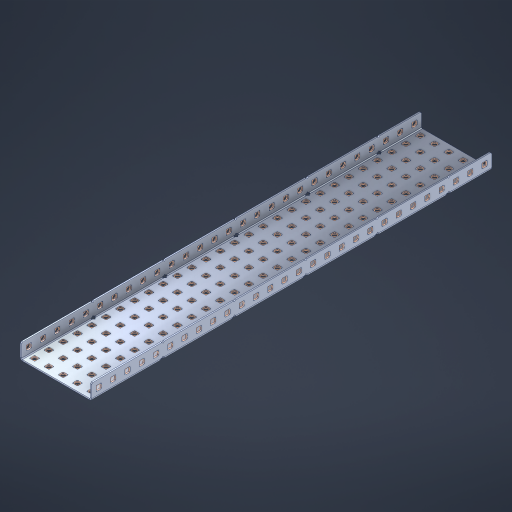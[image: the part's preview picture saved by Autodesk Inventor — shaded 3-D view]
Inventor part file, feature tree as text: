
AUTODESK INVENTOR PART (.ipt)
format: ipt  version: 2023 (Build 270158000, 158)  size: 2,155,008 bytes
history: native  units: in
note: dims shown in document units (in); Inventor stores cm internally (conversion verified against a paired STEP export)
features: other x201, extrude x195, sheet_metal_op x10, sketch x8, mirror x1, pattern_linear x1, chamfer x1
ambient origin geometry x8: Origin, YZ Plane, XZ Plane, XY Plane, X Axis, Y Axis, Z Axis, Center Point
bodies: Solid1 (feature_tree), Body (feature_tree)
feature tree (417):
  other  "Flange Pattern Plane"
  sheet_metal_op  "Flange Pattern"
  sheet_metal_op  "Body Pattern"
  other  "Arc Length"
  mirror  "Notch Mirror"
  pattern_linear  "Notch Pattern"  Spacing1=0.1875in  [1 undecoded]
  chamfer  "End Chamfer"
  extrude  "Half Cut"  Depth=0.0469in
  sketch  "Sketch1"  dims[d0=2.5in]
  other  "Plate1"
  sketch  "Sketch2"  dims[d1=14.0in]
  other  "Plate2"
  sheet_metal_op  "Bend1"
  sheet_metal_op  "Corner1"
  sketch  "Sketch3"  dims[d2=0.0469in]
  other  "Flange Pattern Sketch"
  sketch  "Sketch7"  dims[d3=0.0469in]
  other  "Srf1"
  other  "Srf2"
  sketch  "Sketch8"  dims[d4=0.0234in]
  sketch  "Sketch9"  dims[d5=0.0938in]
  other  "Srf91"
  sheet_metal_op  "Body Pattern Sketch"
  other  "Srf92"
  sketch  "Sketch13"  dims[d6=0.0469in]
  sketch  "Sketch14"  dims[d7=0.5in d8=90.0deg d9=0.0312in d10=0.1875in d11=0.0469in d12=0.0469in d16=0.182in d17=0.02in d18=0.0469in d19=0.0in d20=0.25in d21=0.25in d46=0.172in d47=1.0in d48=0.0in d49=0.182in d50=0.02in d51=0.25in d52=0.25in d53=0.0469in d54=0.0in d55=0.172in d56=1.0in d57=0.0in d60=11.0236in d62=0.5in d63=1.9685in d65=0.5in d85=0.1227in d86=0.1659in d88=0.04in d89=0.0469in d90=0.0in d91=0.04in d92=0.0491in d95=2.5in d96=0.04in d97=0.25in d98=45.0deg d101=0.0in d102=2.497in d131=2.5in d132=11.0236in d134=0.5in d139=0.5in]
  other  "Srf856"
  other  "Srf1310"
  other  "Srf1311"
  other  "Srf1312"
  other  "Srf1376"
  other  "Srf1377"
  other  "Srf1728"
  other  "Srf1755"
  other  "Srf1878"
  other  "Srf1879"
  other  "Srf1880"
  other  "Srf1881"
  other  "Srf1882"
  other  "Srf1883"
  other  "Srf1884"
  other  "Srf1885"
  other  "Srf1886"
  other  "Srf1887"
  other  "Srf1888"
  other  "Srf1889"
  other  "Srf1890"
  other  "Srf1891"
  other  "Srf1892"
  other  "Srf1893"
  other  "Srf1894"
  other  "Srf1895"
  other  "Srf1896"
  other  "Srf1897"
  other  "Srf1898"
  other  "Srf1899"
  other  "Srf1900"
  other  "Srf1901"
  other  "Srf1902"
  other  "Srf1903"
  other  "Srf1904"
  other  "Srf1905"
  other  "Srf1906"
  other  "Srf1942"
  other  "Srf1943"
  other  "Srf1944"
  other  "Srf1945"
  other  "Srf1946"
  other  "Srf1947"
  other  "Srf1948"
  other  "Srf1949"
  other  "Srf1950"
  other  "Srf1951"
  other  "Srf1952"
  other  "Srf1953"
  other  "Srf1954"
  other  "Srf1955"
  other  "Srf1956"
  other  "Srf1957"
  other  "Srf1958"
  other  "Srf1959"
  other  "Srf1960"
  other  "Srf1961"
  other  "Srf1962"
  other  "Srf1963"
  other  "Srf1964"
  other  "Srf1965"
  other  "Srf1966"
  other  "Srf1967"
  other  "Srf1968"
  other  "Srf1969"
  other  "Srf1970"
  other  "Srf2111"
  other  "Srf2112"
  other  "Srf2113"
  other  "Srf2114"
  other  "Srf2115"
  other  "Srf2116"
  other  "Srf2117"
  other  "Srf2118"
  other  "Srf2119"
  other  "Srf2120"
  other  "Srf2121"
  other  "Srf2122"
  other  "Srf2123"
  other  "Srf2124"
  other  "Srf2125"
  other  "Srf2126"
  other  "Srf2127"
  other  "Srf2128"
  other  "Srf2129"
  other  "Srf2130"
  other  "Srf2131"
  other  "Srf2146"
  other  "Srf2147"
  other  "Srf2148"
  other  "Srf2149"
  other  "Srf2150"
  other  "Srf2151"
  other  "Srf2152"
  other  "Srf2153"
  other  "Srf2154"
  other  "Srf2155"
  other  "Srf2156"
  other  "Srf2157"
  other  "Srf2158"
  other  "Srf2159"
  other  "Srf2160"
  other  "Srf2161"
  other  "Srf2162"
  other  "Srf2163"
  other  "Srf2164"
  other  "Srf2165"
  other  "Srf2166"
  other  "Srf2167"
  other  "Srf2168"
  other  "Srf2169"
  other  "Srf2170"
  other  "Srf2171"
  other  "Srf2172"
  other  "Srf2173"
  other  "Srf2174"
  other  "Srf2175"
  other  "Srf2176"
  other  "Srf2177"
  other  "Srf2178"
  other  "Srf2179"
  other  "Srf2180"
  other  "Srf2181"
  other  "Srf2182"
  other  "Srf2183"
  other  "Srf2184"
  other  "Srf2185"
  other  "Srf2186"
  other  "Srf2187"
  other  "Srf2188"
  other  "Srf2189"
  other  "Srf2190"
  other  "Srf2191"
  other  "Srf2192"
  other  "Srf2193"
  other  "Srf2194"
  other  "Srf2195"
  other  "Srf2196"
  other  "Srf2197"
  other  "Srf2198"
  other  "Srf2199"
  other  "Srf2200"
  other  "Srf2201"
  other  "Srf2202"
  other  "Srf2203"
  other  "Srf2204"
  other  "Srf2205"
  other  "Srf2206"
  other  "Srf2207"
  other  "Srf2208"
  other  "Srf2209"
  other  "Srf2210"
  other  "Srf2211"
  other  "Srf2212"
  other  "Srf2213"
  other  "Srf2214"
  other  "Srf2215"
  other  "Srf2216"
  other  "Srf2217"
  other  "Srf2218"
  other  "Srf2219"
  other  "Srf2220"
  other  "Srf2221"
  other  "Srf2222"
  other  "Srf2223"
  other  "Srf2224"
  other  "Srf2225"
  other  "Srf2226"
  other  "Srf2227"
  other  "Srf2228"
  other  "Srf2229"
  other  "Srf2230"
  other  "Srf2231"
  other  "Srf2232"
  other  "Srf2233"
  other  "Srf2234"
  other  "Srf2235"
  other  "Srf2236"
  other  "Srf2237"
  other  "Srf2238"
  other  "Srf2239"
  other  "Srf2240"
  other  "Srf2241"
  other  "Srf2242"
  other  "Srf2243"
  other  "Srf2244"
  other  "Srf2245"
  other  "Srf2246"
  other  "Srf2247"
  other  "Srf2248"
  other  "Srf2249"
  other  "Srf2250"
  sheet_metal_op  "Flange Stamp"
  sheet_metal_op  "Flange Circle"
  sheet_metal_op  "Body Stamp"
  sheet_metal_op  "Body Circle"
  sheet_metal_op  "Notch"
  extrude  "ExtrusionSrf2"  Depth=0.0469in
  extrude  "ExtrusionSrf92"  Depth=2.5in
  extrude  "ExtrusionSrf856"  Depth=0.02in
  extrude  "ExtrusionSrf1310"  Depth=0.0469in
  extrude  "ExtrusionSrf1311"  TaperAngle=0.0deg  [1 undecoded]
  extrude  "ExtrusionSrf1312"  Depth=0.25in
  extrude  "ExtrusionSrf1376"  Depth=0.25in
  extrude  "ExtrusionSrf1377"  Depth=2.5in
  extrude  "ExtrusionSrf1728"  Depth=2.5in TaperAngle=0.0deg
  extrude  "ExtrusionSrf1755"  Depth=2.5in
  extrude  "ExtrusionSrf1878"  Depth=0.02in
  extrude  "ExtrusionSrf1879"  Depth=0.25in
  extrude  "ExtrusionSrf1880"  Depth=0.25in
  extrude  "ExtrusionSrf1881"  Depth=0.0469in
  extrude  "ExtrusionSrf1882"  TaperAngle=0.0deg  [1 undecoded]
  extrude  "ExtrusionSrf1883"  Depth=2.5in
  extrude  "ExtrusionSrf1884"  Depth=2.5in TaperAngle=0.0deg
  extrude  "ExtrusionSrf1885"  Depth=2.5in
  extrude  "ExtrusionSrf1886"  Depth=2.5in
  extrude  "ExtrusionSrf1887"  Depth=2.5in
  extrude  "ExtrusionSrf1888"  Depth=2.5in
  extrude  "ExtrusionSrf1889"  Depth=2.5in
  extrude  "ExtrusionSrf1890"  Depth=0.0469in
  extrude  "ExtrusionSrf1891"  TaperAngle=0.0deg  [1 undecoded]
  extrude  "ExtrusionSrf1892"  Depth=2.5in
  extrude  "ExtrusionSrf1893"  Depth=2.5in
  extrude  "ExtrusionSrf1894"  Depth=2.5in
  extrude  "ExtrusionSrf1895"  Depth=0.25in TaperAngle=45.0deg
  extrude  "ExtrusionSrf1896"  TaperAngle=0.0deg  [1 undecoded]
  extrude  "ExtrusionSrf1897"  Depth=2.5in
  extrude  "ExtrusionSrf1898"  Depth=2.5in
  extrude  "ExtrusionSrf1899"  Depth=2.5in
  extrude  "ExtrusionSrf1900"  Depth=2.5in
  extrude  "ExtrusionSrf1901"  Depth=2.5in
  extrude  "ExtrusionSrf1902"  [1 undecoded]
  extrude  "ExtrusionSrf1903"  [1 undecoded]
  extrude  "ExtrusionSrf1904"  [1 undecoded]
  extrude  "ExtrusionSrf1905"  [1 undecoded]
  extrude  "ExtrusionSrf1906"  [1 undecoded]
  extrude  "ExtrusionSrf1942"  [1 undecoded]
  extrude  "ExtrusionSrf1943"  [1 undecoded]
  extrude  "ExtrusionSrf1944"  [1 undecoded]
  extrude  "ExtrusionSrf1945"  [1 undecoded]
  extrude  "ExtrusionSrf1946"  [1 undecoded]
  extrude  "ExtrusionSrf1947"  [1 undecoded]
  extrude  "ExtrusionSrf1948"  [1 undecoded]
  extrude  "ExtrusionSrf1949"  [1 undecoded]
  extrude  "ExtrusionSrf1950"  [1 undecoded]
  extrude  "ExtrusionSrf1951"  [1 undecoded]
  extrude  "ExtrusionSrf1952"  [1 undecoded]
  extrude  "ExtrusionSrf1953"  [1 undecoded]
  extrude  "ExtrusionSrf1954"  [1 undecoded]
  extrude  "ExtrusionSrf1955"  [1 undecoded]
  extrude  "ExtrusionSrf1956"  [1 undecoded]
  extrude  "ExtrusionSrf1957"  [1 undecoded]
  extrude  "ExtrusionSrf1958"  [1 undecoded]
  extrude  "ExtrusionSrf1959"  [1 undecoded]
  extrude  "ExtrusionSrf1960"  [1 undecoded]
  extrude  "ExtrusionSrf1961"  [1 undecoded]
  extrude  "ExtrusionSrf1962"  [1 undecoded]
  extrude  "ExtrusionSrf1963"  [1 undecoded]
  extrude  "ExtrusionSrf1964"  [1 undecoded]
  extrude  "ExtrusionSrf1965"  [1 undecoded]
  extrude  "ExtrusionSrf1966"  [1 undecoded]
  extrude  "ExtrusionSrf1967"  [1 undecoded]
  extrude  "ExtrusionSrf1968"  [1 undecoded]
  extrude  "ExtrusionSrf1969"  [1 undecoded]
  extrude  "ExtrusionSrf1970"  [1 undecoded]
  extrude  "ExtrusionSrf2111"  [1 undecoded]
  extrude  "ExtrusionSrf2112"  [1 undecoded]
  extrude  "ExtrusionSrf2113"  [1 undecoded]
  extrude  "ExtrusionSrf2114"  [1 undecoded]
  extrude  "ExtrusionSrf2115"  [1 undecoded]
  extrude  "ExtrusionSrf2116"  [1 undecoded]
  extrude  "ExtrusionSrf2117"  [1 undecoded]
  extrude  "ExtrusionSrf2118"  [1 undecoded]
  extrude  "ExtrusionSrf2119"  [1 undecoded]
  extrude  "ExtrusionSrf2120"  [1 undecoded]
  extrude  "ExtrusionSrf2121"  [1 undecoded]
  extrude  "ExtrusionSrf2122"  [1 undecoded]
  extrude  "ExtrusionSrf2123"  [1 undecoded]
  extrude  "ExtrusionSrf2124"  [1 undecoded]
  extrude  "ExtrusionSrf2125"  [1 undecoded]
  extrude  "ExtrusionSrf2126"  [1 undecoded]
  extrude  "ExtrusionSrf2127"  [1 undecoded]
  extrude  "ExtrusionSrf2128"  [1 undecoded]
  extrude  "ExtrusionSrf2129"  [1 undecoded]
  extrude  "ExtrusionSrf2130"  [1 undecoded]
  extrude  "ExtrusionSrf2131"  [1 undecoded]
  extrude  "ExtrusionSrf2146"  [1 undecoded]
  extrude  "ExtrusionSrf2147"  [1 undecoded]
  extrude  "ExtrusionSrf2148"  [1 undecoded]
  extrude  "ExtrusionSrf2149"  [1 undecoded]
  extrude  "ExtrusionSrf2150"  [1 undecoded]
  extrude  "ExtrusionSrf2151"  [1 undecoded]
  extrude  "ExtrusionSrf2152"  [1 undecoded]
  extrude  "ExtrusionSrf2153"  [1 undecoded]
  extrude  "ExtrusionSrf2154"  [1 undecoded]
  extrude  "ExtrusionSrf2155"  [1 undecoded]
  extrude  "ExtrusionSrf2156"  [1 undecoded]
  extrude  "ExtrusionSrf2157"  [1 undecoded]
  extrude  "ExtrusionSrf2158"  [1 undecoded]
  extrude  "ExtrusionSrf2159"  [1 undecoded]
  extrude  "ExtrusionSrf2160"  [1 undecoded]
  extrude  "ExtrusionSrf2161"  [1 undecoded]
  extrude  "ExtrusionSrf2162"  [1 undecoded]
  extrude  "ExtrusionSrf2163"  [1 undecoded]
  extrude  "ExtrusionSrf2164"  [1 undecoded]
  extrude  "ExtrusionSrf2165"  [1 undecoded]
  extrude  "ExtrusionSrf2166"  [1 undecoded]
  extrude  "ExtrusionSrf2167"  [1 undecoded]
  extrude  "ExtrusionSrf2168"  [1 undecoded]
  extrude  "ExtrusionSrf2169"  [1 undecoded]
  extrude  "ExtrusionSrf2170"  [1 undecoded]
  extrude  "ExtrusionSrf2171"  [1 undecoded]
  extrude  "ExtrusionSrf2172"  [1 undecoded]
  extrude  "ExtrusionSrf2173"  [1 undecoded]
  extrude  "ExtrusionSrf2174"  [1 undecoded]
  extrude  "ExtrusionSrf2175"  [1 undecoded]
  extrude  "ExtrusionSrf2176"  [1 undecoded]
  extrude  "ExtrusionSrf2177"  [1 undecoded]
  extrude  "ExtrusionSrf2178"  [1 undecoded]
  extrude  "ExtrusionSrf2179"  [1 undecoded]
  extrude  "ExtrusionSrf2180"  [1 undecoded]
  extrude  "ExtrusionSrf2181"  [1 undecoded]
  extrude  "ExtrusionSrf2182"  [1 undecoded]
  extrude  "ExtrusionSrf2183"  [1 undecoded]
  extrude  "ExtrusionSrf2184"  [1 undecoded]
  extrude  "ExtrusionSrf2185"  [1 undecoded]
  extrude  "ExtrusionSrf2186"  [1 undecoded]
  extrude  "ExtrusionSrf2187"  [1 undecoded]
  extrude  "ExtrusionSrf2188"  [1 undecoded]
  extrude  "ExtrusionSrf2189"  [1 undecoded]
  extrude  "ExtrusionSrf2190"  [1 undecoded]
  extrude  "ExtrusionSrf2191"  [1 undecoded]
  extrude  "ExtrusionSrf2192"  [1 undecoded]
  extrude  "ExtrusionSrf2193"  [1 undecoded]
  extrude  "ExtrusionSrf2194"  [1 undecoded]
  extrude  "ExtrusionSrf2195"  [1 undecoded]
  extrude  "ExtrusionSrf2196"  [1 undecoded]
  extrude  "ExtrusionSrf2197"  [1 undecoded]
  extrude  "ExtrusionSrf2198"  [1 undecoded]
  extrude  "ExtrusionSrf2199"  [1 undecoded]
  extrude  "ExtrusionSrf2200"  [1 undecoded]
  extrude  "ExtrusionSrf2201"  [1 undecoded]
  extrude  "ExtrusionSrf2202"  [1 undecoded]
  extrude  "ExtrusionSrf2203"  [1 undecoded]
  extrude  "ExtrusionSrf2204"  [1 undecoded]
  extrude  "ExtrusionSrf2205"  [1 undecoded]
  extrude  "ExtrusionSrf2206"  [1 undecoded]
  extrude  "ExtrusionSrf2207"  [1 undecoded]
  extrude  "ExtrusionSrf2208"  [1 undecoded]
  extrude  "ExtrusionSrf2209"  [1 undecoded]
  extrude  "ExtrusionSrf2210"  [1 undecoded]
  extrude  "ExtrusionSrf2211"  [1 undecoded]
  extrude  "ExtrusionSrf2212"  [1 undecoded]
  extrude  "ExtrusionSrf2213"  [1 undecoded]
  extrude  "ExtrusionSrf2214"  [1 undecoded]
  extrude  "ExtrusionSrf2215"  [1 undecoded]
  extrude  "ExtrusionSrf2216"  [1 undecoded]
  extrude  "ExtrusionSrf2217"  [1 undecoded]
  extrude  "ExtrusionSrf2218"  [1 undecoded]
  extrude  "ExtrusionSrf2219"  [1 undecoded]
  extrude  "ExtrusionSrf2220"  [1 undecoded]
  extrude  "ExtrusionSrf2221"  [1 undecoded]
  extrude  "ExtrusionSrf2222"  [1 undecoded]
  extrude  "ExtrusionSrf2223"  [1 undecoded]
  extrude  "ExtrusionSrf2224"  [1 undecoded]
  extrude  "ExtrusionSrf2225"  [1 undecoded]
  extrude  "ExtrusionSrf2226"  [1 undecoded]
  extrude  "ExtrusionSrf2227"  [1 undecoded]
  extrude  "ExtrusionSrf2228"  [1 undecoded]
  extrude  "ExtrusionSrf2229"  [1 undecoded]
  extrude  "ExtrusionSrf2230"  [1 undecoded]
  extrude  "ExtrusionSrf2231"  [1 undecoded]
  extrude  "ExtrusionSrf2232"  [1 undecoded]
  extrude  "ExtrusionSrf2233"  [1 undecoded]
  extrude  "ExtrusionSrf2234"  [1 undecoded]
  extrude  "ExtrusionSrf2235"  [1 undecoded]
  extrude  "ExtrusionSrf2236"  [1 undecoded]
  extrude  "ExtrusionSrf2237"  [1 undecoded]
  extrude  "ExtrusionSrf2238"  [1 undecoded]
  extrude  "ExtrusionSrf2239"  [1 undecoded]
  extrude  "ExtrusionSrf2240"  [1 undecoded]
  extrude  "ExtrusionSrf2241"  [1 undecoded]
  extrude  "ExtrusionSrf2242"  [1 undecoded]
  extrude  "ExtrusionSrf2243"  [1 undecoded]
  extrude  "ExtrusionSrf2244"  [1 undecoded]
  extrude  "ExtrusionSrf2245"  [1 undecoded]
  extrude  "ExtrusionSrf2246"  [1 undecoded]
  extrude  "ExtrusionSrf2247"  [1 undecoded]
  extrude  "ExtrusionSrf2248"  [1 undecoded]
  extrude  "ExtrusionSrf2249"  [1 undecoded]
  extrude  "ExtrusionSrf2250"  [1 undecoded]
note: 165 required parameter values undecoded (feature->parameter linkage not recoverable at this tier; creation-order binding heuristic only, values carry confidence <= 0.55)
